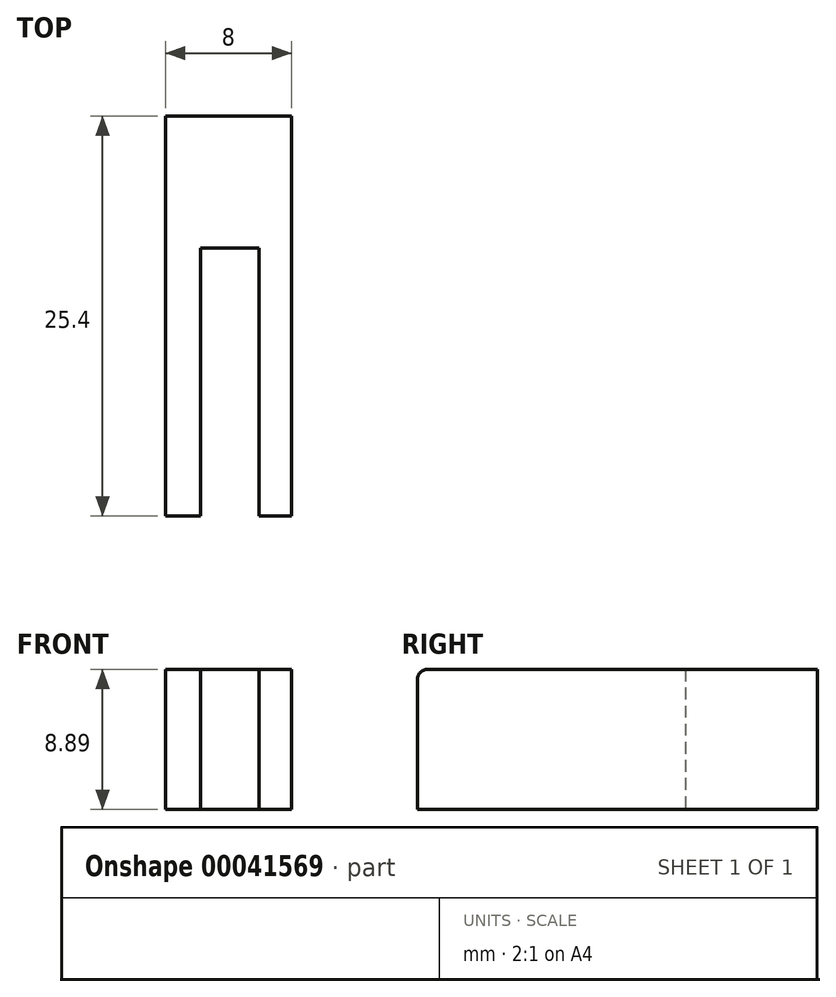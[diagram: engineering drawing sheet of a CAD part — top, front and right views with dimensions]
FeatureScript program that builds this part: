
annotation { "Feature Type Name" : "Feature", "Feature Type Description" : "" }
export const myFeature = defineFeature(function(context is Context, id is Id, definition is map)
    precondition{}
    {
        {
            var Q0;
            Q0=qCreatedBy(makeId("Right.planeOp"),FACE);
            var sketch = newSketch(context, id + "F0", { "sketchPlane" : qUnion([Q0])});
            skLineSegment(sketch, "E0.bottom", {"start": v(-6.46, 8.89) * mm, "end": v(18.3, 8.89) * mm});
            skLineSegment(sketch, "E0.top", {"start": v(-7.1, 0) * mm, "end": v(18.3, 0) * mm});
            skLineSegment(sketch, "E0.left", {"start": v(-7.1, 8.25) * mm, "end": v(-7.1, 0) * mm});
            skLineSegment(sketch, "E0.right", {"start": v(18.3, 8.89) * mm, "end": v(18.3, 0) * mm});
            skPoint(sketch, "E1.visualSharp", {"position": v(-7.1, 8.89) * mm});
            skArc(sketch, "E1.filletArc", {"start": v(-6.46, 8.89) * mm, "mid": v(-6.9, 8.7) * mm, "end": v(-7.1, 8.25) * mm});
            skSolve(sketch);
        }
        {
            var Q0;
            Q0=makeQuery(id+"F0.imprint","IMPRINT",FACE,{"disambiguationData":[TD([[makeQuery(id+"F0.imprint","IMPRINT",EDGE,{"derivedFrom":sQuery(id+"F0.wireOp",EDGE,"E0.bottom")}),-1.0]])]});
            extrude(context, id + "F1", {"entities" : qUnion([Q0]), "depth" : 8 * mm});
        }
        {
            var Q0;
            Q0=qCreatedBy(makeId("Top.planeOp"),FACE);
            var sketch = newSketch(context, id + "F2", { "sketchPlane" : qUnion([Q0])});
            skLineSegment(sketch, "E2.bottom", {"start": v(2.22, 9.92) * mm, "end": v(5.93, 9.92) * mm});
            skLineSegment(sketch, "E2.top", {"start": v(2.22, -10.08) * mm, "end": v(5.93, -10.08) * mm});
            skLineSegment(sketch, "E2.left", {"start": v(2.22, 9.92) * mm, "end": v(2.22, -10.08) * mm});
            skLineSegment(sketch, "E2.right", {"start": v(5.93, 9.92) * mm, "end": v(5.93, -10.08) * mm});
            skSolve(sketch);
        }
        {
            var Q0;
            Q0 = qSketchRegion(id + "F2", true);
            extrude(context, id + "F3", {"entities" : qUnion([Q0]), "operationType" : NewBodyOperationType.REMOVE, "depth" : 9.3 * mm});
        }
    });
